# Revit family: Thorn Chalice 3 MSF 180
name_source: partatom
category: Lighting Fixtures
revit_build: Autodesk Revit 2018 (Build: 20170223_1515(x64)
units: mm (PartAtom-declared; Revit-internal decimal feet)

## family parameters
Cut with Voids When Loaded = No
Host = Face
Light Source = Yes
Part Type = Normal
Room Calculation Point = No
Round Connector Dimension = Use Diameter
Shared = No

## types (2) — shared parameters
Apparent Load = 18 VA
CAD Model Ref Link = http://www.thornlighting.com
Color Filter = 16777215
Default Elevation = 1219 mm
Dim Details = DALI2 standby power 0.2W
Dimming Lamp Color Temperature Shift = <None>
Earth Present = Yes
Earthing Class = 1
Emit Shape Visible in Rendering = No
Emit from Circle Diameter = 100 mm  [stored 0.328084 ft]
Height = 94 mm
Hz = 50 Hz
Lamp = LED
Lamp Position = std
Lamp Type = LED
Length = 172 mm
Manufacturer = Thorn Lighting
Mounting Type = Recessed
No of Lamps = 1
No of Sources = 1
Placement Type = Ceiling
Power Factor = 0.93
Spares List = http://www.thornlighting.com
Tilt Angle = -90.00°
Web Link to Docs = http://www.thornlighting.com
Width = 172 mm
zero-valued in all types: Cost

## per-type parameters (varying)
| type | Circuit Watts | IK Rating | IP Rating | Mass | Photometric Web File | Rating | Sap Code |
| CHAL3 150 2000-840 HFIX RMB | 16 W | IK09 | IP20 / IP54 | 0.69 | 92989222_(STD).IES | 16.5 | 92989222 |
| CHAL3 150 2000-840 HFIX RSB | 17 W | IK06 | IP43 | 2.67 | 92989216_(STD).IES | 16.9 | 92994987 |

note: [stored X ft] marks values corroborated as IEEE doubles in the binary element streams (Revit-internal decimal feet)

## geometry (parser evidence)
native form markers: Sweep x1
no freeform markers — native parametric forms only
